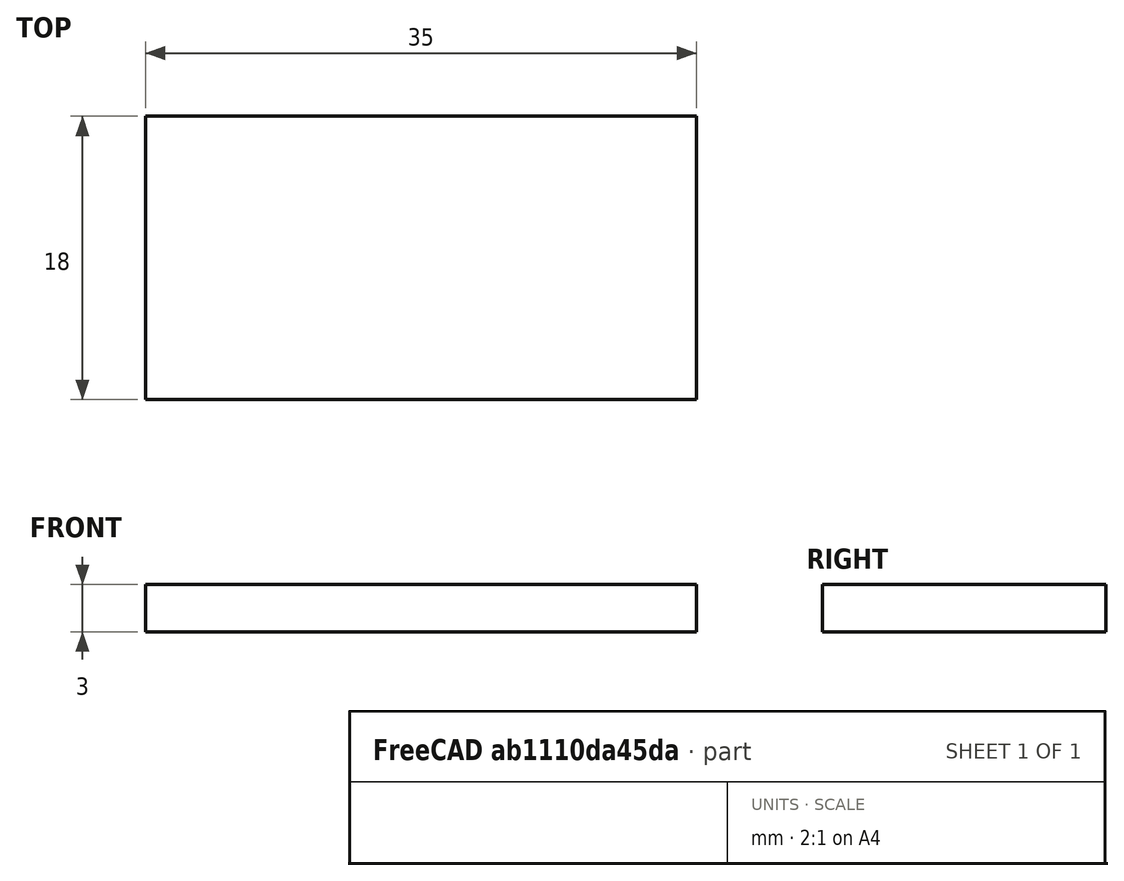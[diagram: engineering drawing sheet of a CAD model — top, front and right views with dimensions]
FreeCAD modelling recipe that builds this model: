
FCSTD DOCUMENT  (FreeCAD 0.19R)
Label: arduino_pro_micro
License: All rights reserved
LicenseURL: http://en.wikipedia.org/wiki/All_rights_reserved
objects: Sketcher::SketchObject×1, PartDesign::Pad×1, PartDesign::Body×1
note: 4 computed .brp shape members not serialized (recipe doc carries the construction recipe); baked Part::Feature solids carry a one-line shape summary decoded from their .brp

FEATURE [Sketcher::SketchObject] Sketch
  MapMode = 5
  Support = -> [XY_Plane]
  sketch-geometry (4):
    g0: LineSegment StartX=0 StartY=0 StartZ=0 EndX=35 EndY=0 EndZ=0
    g1: LineSegment StartX=35 StartY=0 StartZ=0 EndX=35 EndY=18 EndZ=0
    g2: LineSegment StartX=35 StartY=18 StartZ=0 EndX=0 EndY=18 EndZ=0
    g3: LineSegment StartX=0 StartY=18 StartZ=0 EndX=0 EndY=0 EndZ=0
  constraints (11):
    c: Coincident(g0,g1)
    c: Coincident(g1,g2)
    c: Coincident(g2,g3)
    c: Coincident(g3,g0)
    c: Horizontal(g0)
    c: Horizontal(g2)
    c: Vertical(g1)
    c: Vertical(g3)
    c: Coincident(g0,g-1)
    c: DistanceX(g0,g0) = 35
    c: DistanceY(g1,g1) = 18
FEATURE [PartDesign::Pad] Pad
  Length = 3
  Length2 = 100
  Profile = -> Sketch
  Type = 0
FEATURE [PartDesign::Body] Body
  Group = -> [Sketch,Pad]
  Origin = -> Origin
  Tip = -> Pad
